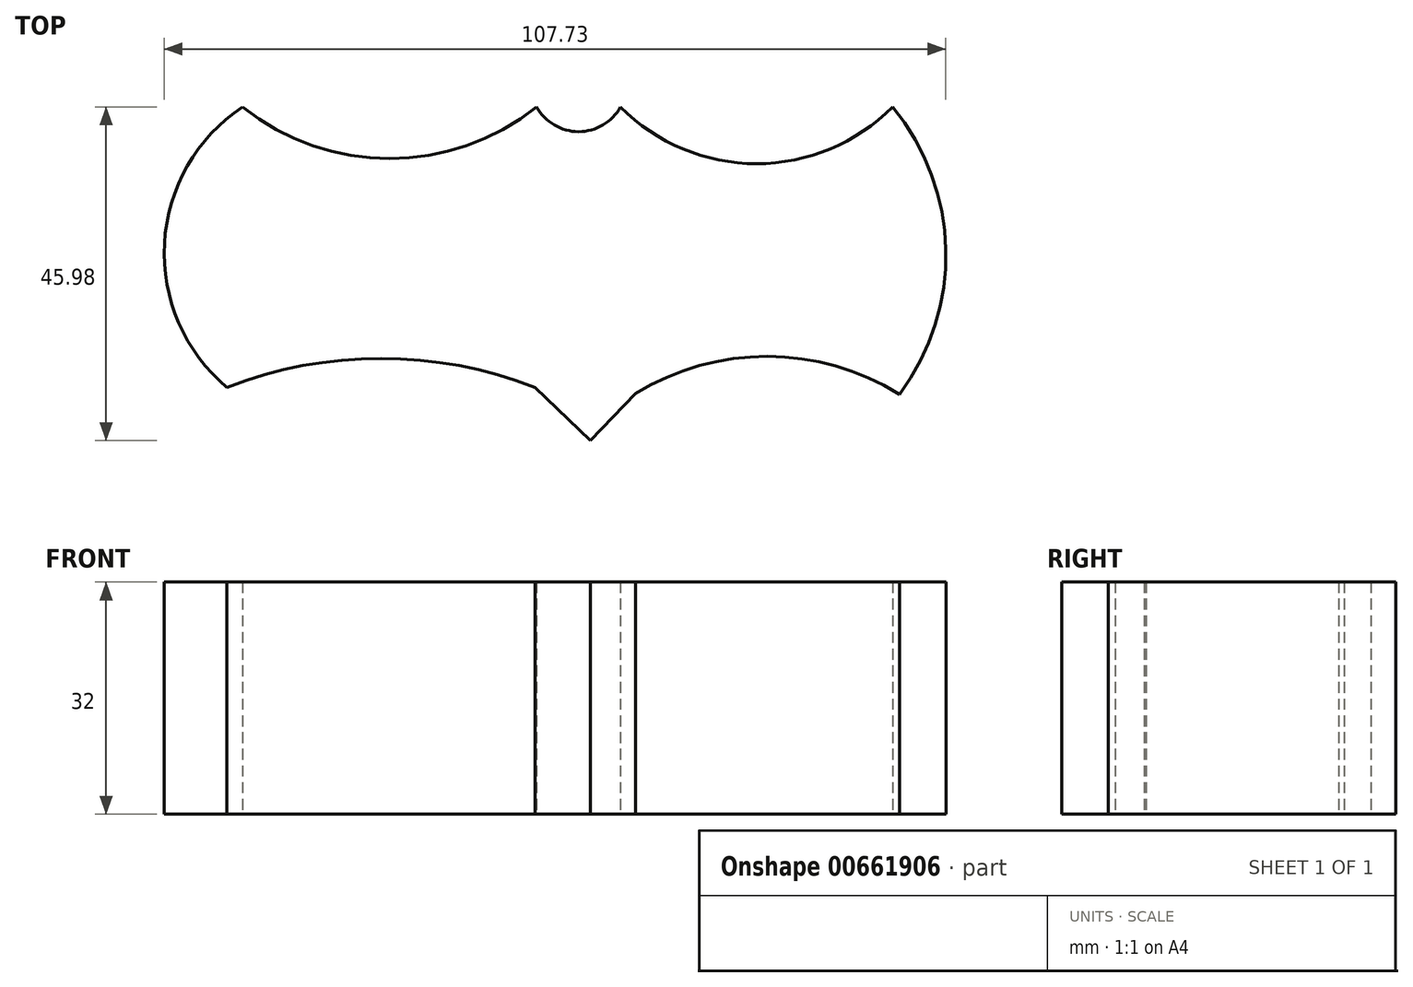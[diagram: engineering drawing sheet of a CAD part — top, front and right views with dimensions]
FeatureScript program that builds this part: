
annotation { "Feature Type Name" : "Feature", "Feature Type Description" : "" }
export const myFeature = defineFeature(function(context is Context, id is Id, definition is map)
    precondition{}
    {
        {
            var Q0;
            Q0=qCreatedBy(makeId("Top.planeOp"),FACE);
            var sketch = newSketch(context, id + "F0", { "sketchPlane" : qUnion([Q0])});
            skArc(sketch, "E0", {"start": v(42.56, -19.22) * mm, "mid": v(48.96, 0.75) * mm, "end": v(41.61, 20.4) * mm});
            skArc(sketch, "E1", {"start": v(4.13, 20.4) * mm, "mid": v(22.87, 12.57) * mm, "end": v(41.61, 20.4) * mm});
            skArc(sketch, "E2", {"start": v(-7.43, 20.4) * mm, "mid": v(-1.65, 16.98) * mm, "end": v(4.13, 20.4) * mm});
            skArc(sketch, "E3", {"start": v(-47.98, 20.4) * mm, "mid": v(-27.7, 13.28) * mm, "end": v(-7.43, 20.4) * mm});
            skArc(sketch, "E4", {"start": v(-47.98, 20.4) * mm, "mid": v(-58.73, 1.6) * mm, "end": v(-50.1, -18.27) * mm});
            skArc(sketch, "E5", {"start": v(-7.66, -18.27) * mm, "mid": v(-28.88, -14.26) * mm, "end": v(-50.1, -18.27) * mm});
            skLineSegment(sketch, "E6", {"start": v(-7.66, -18.27) * mm, "end": v(0, -25.59) * mm});
            skLineSegment(sketch, "E7", {"start": v(0, -25.59) * mm, "end": v(6.18, -19.11) * mm});
            skArc(sketch, "E8", {"start": v(42.56, -19.22) * mm, "mid": v(24.39, -14) * mm, "end": v(6.18, -19.11) * mm});
            skSolve(sketch);
        }
        {
            var Q0;
            Q0=makeQuery(id+"F0.imprint","IMPRINT",FACE,{"disambiguationData":[TD([[makeQuery(id+"F0.imprint","IMPRINT",EDGE,{"derivedFrom":sQuery(id+"F0.wireOp",EDGE,"E0")}),1.0]])]});
            extrude(context, id + "F1", {"entities" : qUnion([Q0]), "depth" : 25 * mm, "offsetDistance" : 25 * mm});
        }
        {
            var Q0;
            Q0=makeQuery(id+"F1.opExtrude","CAP_FACE",FACE,{"disambiguationData":[OSD([sQuery(id+"F0.wireOp",EDGE,"E0"),sQuery(id+"F0.wireOp",EDGE,"E1"),sQuery(id+"F0.wireOp",EDGE,"E2"),sQuery(id+"F0.wireOp",EDGE,"E3"),sQuery(id+"F0.wireOp",EDGE,"E4"),sQuery(id+"F0.wireOp",EDGE,"E5"),sQuery(id+"F0.wireOp",EDGE,"E6"),sQuery(id+"F0.wireOp",EDGE,"E7"),sQuery(id+"F0.wireOp",EDGE,"E8")])],"isStart":false});
            extrude(context, id + "F2", {"entities" : qUnion([Q0]), "operationType" : NewBodyOperationType.ADD, "depth" : 7 * mm, "offsetDistance" : 25 * mm});
        }
    });
